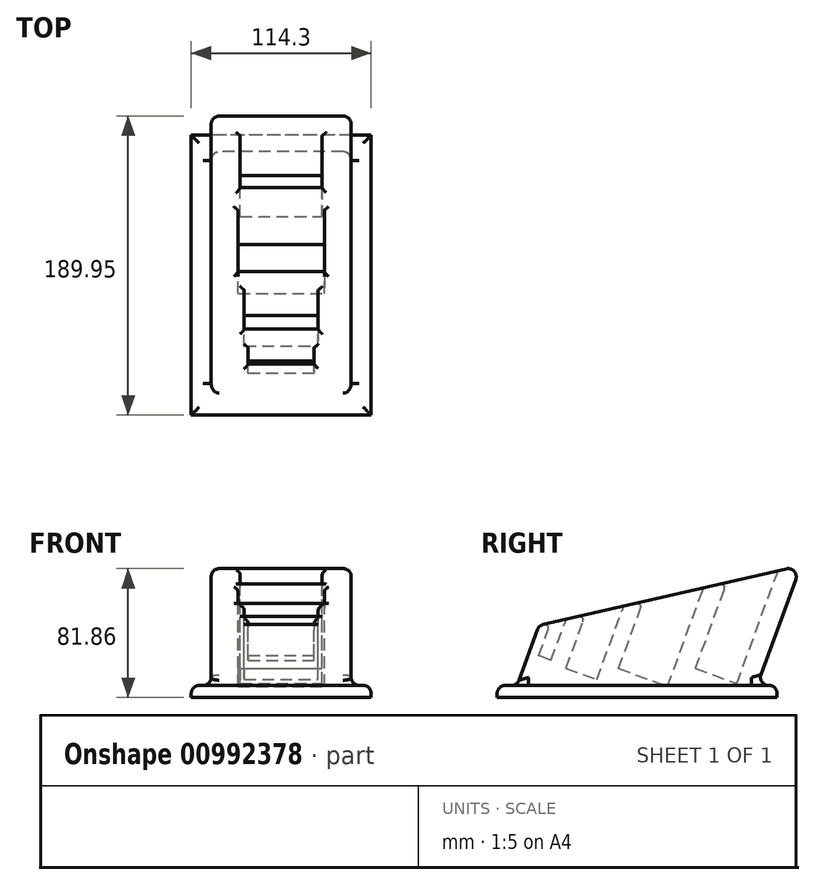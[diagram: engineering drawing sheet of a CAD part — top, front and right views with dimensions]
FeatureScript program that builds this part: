
annotation { "Feature Type Name" : "Feature", "Feature Type Description" : "" }
export const myFeature = defineFeature(function(context is Context, id is Id, definition is map)
    precondition{}
    {
        {
            var Q0;
            Q0=qCreatedBy(makeId("Right.planeOp"),FACE);
            var sketch = newSketch(context, id + "F0", { "sketchPlane" : qUnion([Q0])});
            skLineSegment(sketch, "E0.bottom", {"start": v(-88.9, 0) * mm, "end": v(88.9, 0) * mm});
            skLineSegment(sketch, "E0.left", {"start": v(-88.9, 0) * mm, "end": v(-88.9, 7.62) * mm});
            skLineSegment(sketch, "E0.right", {"start": v(88.9, 0) * mm, "end": v(88.9, 7.62) * mm});
            skLineSegment(sketch, "E1", {"start": v(-88.9, 7.62) * mm, "end": v(88.9, 7.62) * mm});
            skLineSegment(sketch, "E2", {"start": v(76.2, 7.62) * mm, "end": v(103.93, 83.82) * mm});
            skLineSegment(sketch, "E3", {"start": v(-76.2, 7.62) * mm, "end": v(-62.33, 45.72) * mm});
            skLineSegment(sketch, "E4", {"start": v(-62.33, 45.72) * mm, "end": v(103.93, 83.82) * mm});
            skSolve(sketch);
        }
        {
            var Q0;
            Q0=makeQuery(id+"F0.imprint","IMPRINT",FACE,{"disambiguationData":[TD([[makeQuery(id+"F0.imprint","IMPRINT",EDGE,{"derivedFrom":sQuery(id+"F0.wireOp",EDGE,"E0.bottom")}),1.0]])]});
            extrude(context, id + "F1", {"entities" : qUnion([Q0]), "depth" : 114.3 * mm, "offsetDistance" : 25.4 * mm, "symmetric" : true});
        }
        {
            var Q0;
            {var subQ0=sQuery(id+"F0.wireOp",EDGE,"E2");Q0=makeQuery(id+"F0.imprint","IMPRINT",FACE,{"disambiguationData":[TD([[makeQuery(id+"F0.imprint","IMPRINT",EDGE,{"derivedFrom":subQ0}),1.0]])]});}
            extrude(context, id + "F2", {"entities" : qUnion([Q0]), "operationType" : NewBodyOperationType.ADD, "depth" : 88.9 * mm, "offsetDistance" : 25.4 * mm, "symmetric" : true});
        }
        {
            var Q0;
            Q0=makeQuery(id+"F2.opExtrude","SWEPT_EDGE",EDGE,{"disambiguationData":[OSD([sQuery(id+"F0.wireOp",EDGE,"E2"),sQuery(id+"F0.wireOp",EDGE,"E4")])]});
            var Q1;
            Q1=sQuery(id+"F0.wireOp",EDGE,"E2");
            cPlane(context, id + "F3", {"entities" : qUnion([Q0, Q1]), "cplaneType" : CPlaneType.LINE_ANGLE, "offset" : 25.4 * mm, "angle" : 90 * degree, "width" : 152.4 * mm, "height" : 152.4 * mm});
        }
        {
            var Q0;
            Q0=makeQuery(id+"F2.opExtrude","SWEPT_FACE",FACE,{"disambiguationData":[OSD([sQuery(id+"F0.wireOp",EDGE,"E4")])]});
            var sketch = newSketch(context, id + "F4", { "sketchPlane" : qUnion([Q0])});
            skLineSegment(sketch, "E5.bottom", {"start": v(20.96, -42.93) * mm, "end": v(-20.96, -42.93) * mm});
            skSolve(sketch);
        }
        {
            var Q0;
            Q0=qCreatedBy(id+"F3.planeOp",FACE);
            var sketch = newSketch(context, id + "F5", { "sketchPlane" : qUnion([Q0])});
            skLineSegment(sketch, "E6.0", {"start": v(20.96, 67.81) * mm, "end": v(-20.96, 67.81) * mm});
            skLineSegment(sketch, "E7", {"start": v(-20.96, 67.81) * mm, "end": v(-20.96, 59.43) * mm});
            skLineSegment(sketch, "E8", {"start": v(-20.96, 59.43) * mm, "end": v(20.96, 59.43) * mm});
            skLineSegment(sketch, "E9", {"start": v(20.95, 59.43) * mm, "end": v(20.95, 67.81) * mm});
            skSolve(sketch);
        }
        {
            var Q0;
            Q0 = qSketchRegion(id + "F5", true);
            extrude(context, id + "F6", {"entities" : qUnion([Q0]), "operationType" : NewBodyOperationType.REMOVE, "depth" : 110.74 * mm, "offsetDistance" : 25.4 * mm});
        }
        {
            var Q0;
            {var subQ0=sQuery(id+"F0.wireOp",EDGE,"E4");Q0=makeQuery(id+"F4.imprint","IMPRINT",FACE,{"disambiguationData":[TD([[makeQuery(id+"F4.imprint","IMPRINT",EDGE,{"derivedFrom":makeQuery(id+"F2.opExtrude","CAP_EDGE",EDGE,{"disambiguationData":[OSD([subQ0])],"isStart":true})}),-1.0]])]});}
            var sketch = newSketch(context, id + "F7", { "sketchPlane" : qUnion([Q0])});
            skLineSegment(sketch, "E10", {"start": v(-23.5, -20.24) * mm, "end": v(23.5, -20.24) * mm});
            skSolve(sketch);
        }
        {
            var Q0;
            Q0=qCreatedBy(id+"F3.planeOp",FACE);
            var sketch = newSketch(context, id + "F8", { "sketchPlane" : qUnion([Q0])});
            skLineSegment(sketch, "E11.0", {"start": v(-23.5, 48.77) * mm, "end": v(23.5, 48.77) * mm});
            skLineSegment(sketch, "E12", {"start": v(-23.5, 48.77) * mm, "end": v(-23.5, 27.94) * mm});
            skLineSegment(sketch, "E13", {"start": v(-23.5, 27.94) * mm, "end": v(23.5, 27.94) * mm});
            skLineSegment(sketch, "E14", {"start": v(23.5, 27.94) * mm, "end": v(23.5, 48.77) * mm});
            skSolve(sketch);
        }
        {
            var Q0;
            Q0 = qSketchRegion(id + "F8", true);
            extrude(context, id + "F9", {"entities" : qUnion([Q0]), "operationType" : NewBodyOperationType.REMOVE, "depth" : 112.27 * mm, "offsetDistance" : 25.4 * mm});
        }
        {
            var Q0;
            {var subQ0=sQuery(id+"F0.wireOp",EDGE,"E4");Q0=makeQuery(id+"F4.imprint","IMPRINT",FACE,{"disambiguationData":[TD([[makeQuery(id+"F4.imprint","IMPRINT",EDGE,{"derivedFrom":makeQuery(id+"F2.opExtrude","CAP_EDGE",EDGE,{"disambiguationData":[OSD([subQ0])],"isStart":true})}),-1.0]])]});}
            var sketch = newSketch(context, id + "F10", { "sketchPlane" : qUnion([Q0])});
            skLineSegment(sketch, "E15", {"start": v(-27.43, 17.27) * mm, "end": v(27.43, 17.27) * mm});
            skLineSegment(sketch, "E16", {"start": v(0, 85.1) * mm, "end": v(0, -16.61) * mm, "construction": true});
            skSolve(sketch);
        }
        {
            var Q0;
            Q0=qCreatedBy(id+"F3.planeOp",FACE);
            var sketch = newSketch(context, id + "F11", { "sketchPlane" : qUnion([Q0])});
            skLineSegment(sketch, "E17.0", {"start": v(-27.43, 17.28) * mm, "end": v(27.43, 17.28) * mm});
            skLineSegment(sketch, "E18", {"start": v(-27.43, 17.28) * mm, "end": v(-27.43, -15.74) * mm});
            skLineSegment(sketch, "E19", {"start": v(-27.43, -15.74) * mm, "end": v(27.43, -15.74) * mm});
            skLineSegment(sketch, "E20", {"start": v(27.43, -15.74) * mm, "end": v(27.43, 17.28) * mm});
            skSolve(sketch);
        }
        {
            var Q0;
            Q0 = qSketchRegion(id + "F11", true);
            extrude(context, id + "F12", {"entities" : qUnion([Q0]), "operationType" : NewBodyOperationType.REMOVE, "depth" : 101.1 * mm, "offsetDistance" : 25.4 * mm});
        }
        {
            var Q0;
            {var subQ0=sQuery(id+"F0.wireOp",EDGE,"E4");Q0=makeQuery(id+"F4.imprint","IMPRINT",FACE,{"disambiguationData":[TD([[makeQuery(id+"F4.imprint","IMPRINT",EDGE,{"derivedFrom":makeQuery(id+"F2.opExtrude","CAP_EDGE",EDGE,{"disambiguationData":[OSD([subQ0])],"isStart":true})}),-1.0]])]});}
            var sketch = newSketch(context, id + "F13", { "sketchPlane" : qUnion([Q0])});
            skLineSegment(sketch, "E21", {"start": v(-26.04, 71.84) * mm, "end": v(26.04, 71.84) * mm});
            skSolve(sketch);
        }
        {
            var Q0;
            Q0=qCreatedBy(id+"F3.planeOp",FACE);
            var sketch = newSketch(context, id + "F14", { "sketchPlane" : qUnion([Q0])});
            skLineSegment(sketch, "E22.0", {"start": v(-26.04, -28.54) * mm, "end": v(26.04, -28.54) * mm});
            skLineSegment(sketch, "E23", {"start": v(-26.03, -28.54) * mm, "end": v(-26.03, -56.48) * mm});
            skLineSegment(sketch, "E24", {"start": v(-26.03, -56.48) * mm, "end": v(26.04, -56.48) * mm});
            skLineSegment(sketch, "E25", {"start": v(26.04, -56.48) * mm, "end": v(26.04, -28.54) * mm});
            skSolve(sketch);
        }
        {
            var Q0;
            Q0 = qSketchRegion(id + "F14", true);
            extrude(context, id + "F15", {"entities" : qUnion([Q0]), "operationType" : NewBodyOperationType.REMOVE, "depth" : 84.33 * mm, "offsetDistance" : 25.4 * mm});
        }
        {
            var Q0;
            Q0=makeQuery(id+"F2.opExtrude","CAP_EDGE",EDGE,{"disambiguationData":[OSD([sQuery(id+"F0.wireOp",EDGE,"E4")])],"isStart":false});
            var Q1;
            Q1=makeQuery(id+"F2.opExtrude","SWEPT_EDGE",EDGE,{"disambiguationData":[OSD([sQuery(id+"F0.wireOp",EDGE,"E3"),sQuery(id+"F0.wireOp",EDGE,"E4")])]});
            var Q2;
            Q2=makeQuery(id+"F2.opExtrude","CAP_FACE",FACE,{"disambiguationData":[OSD([sQuery(id+"F0.wireOp",EDGE,"E1"),sQuery(id+"F0.wireOp",EDGE,"E2"),sQuery(id+"F0.wireOp",EDGE,"E3"),sQuery(id+"F0.wireOp",EDGE,"E4")])],"isStart":false});
            var Q3;
            Q3=makeQuery(id+"F2.opExtrude","SWEPT_EDGE",EDGE,{"disambiguationData":[OSD([sQuery(id+"F0.wireOp",EDGE,"E2"),sQuery(id+"F0.wireOp",EDGE,"E4")])]});
            var Q4;
            Q4=makeQuery(id+"F2.opExtrude","CAP_FACE",FACE,{"disambiguationData":[OSD([sQuery(id+"F0.wireOp",EDGE,"E1"),sQuery(id+"F0.wireOp",EDGE,"E2"),sQuery(id+"F0.wireOp",EDGE,"E3"),sQuery(id+"F0.wireOp",EDGE,"E4")])],"isStart":true});
            var Q5;
            Q5=makeQuery(id+"F1.opExtrude","SWEPT_FACE",FACE,{"disambiguationData":[OSD([sQuery(id+"F0.wireOp",EDGE,"E1")])]});
            fillet(context, id + "F16", {"entities" : qUnion([Q0, Q1, Q2, Q3, Q4, Q5]), "tangentPropagation" : true, "radius" : 5.08 * mm, "defaultsChanged" : false, "vertexSettings" : [], "allowEdgeOverflow" : false});
        }
        {
            var Q0;
            Q0=makeQuery(id+"F15.boolean.opBoolean","INTERSECT",EDGE,{"derivedFrom":[makeQuery(id+"F2.opExtrude","SWEPT_FACE",FACE,{"disambiguationData":[OSD([sQuery(id+"F0.wireOp",EDGE,"E4")])]}),makeQuery(id+"F15.opExtrude","SWEPT_FACE",FACE,{"disambiguationData":[OSD([sQuery(id+"F14.wireOp",EDGE,"E22.0")])]})]});
            var Q1;
            Q1=makeQuery(id+"F15.boolean.opBoolean","INTERSECT",EDGE,{"derivedFrom":[makeQuery(id+"F2.opExtrude","SWEPT_FACE",FACE,{"disambiguationData":[OSD([sQuery(id+"F0.wireOp",EDGE,"E4")])]}),makeQuery(id+"F15.opExtrude","SWEPT_FACE",FACE,{"disambiguationData":[OSD([sQuery(id+"F14.wireOp",EDGE,"E24")])]})]});
            var Q2;
            Q2=makeQuery(id+"F15.boolean.opBoolean","INTERSECT",EDGE,{"derivedFrom":[makeQuery(id+"F2.opExtrude","SWEPT_FACE",FACE,{"disambiguationData":[OSD([sQuery(id+"F0.wireOp",EDGE,"E4")])]}),makeQuery(id+"F15.opExtrude","SWEPT_FACE",FACE,{"disambiguationData":[OSD([sQuery(id+"F14.wireOp",EDGE,"E25")])]})]});
            var Q3;
            Q3=makeQuery(id+"F15.boolean.opBoolean","INTERSECT",EDGE,{"derivedFrom":[makeQuery(id+"F2.opExtrude","SWEPT_FACE",FACE,{"disambiguationData":[OSD([sQuery(id+"F0.wireOp",EDGE,"E4")])]}),makeQuery(id+"F15.opExtrude","SWEPT_FACE",FACE,{"disambiguationData":[OSD([sQuery(id+"F14.wireOp",EDGE,"E23")])]})]});
            var Q4;
            Q4=makeQuery(id+"F12.boolean.opBoolean","INTERSECT",EDGE,{"derivedFrom":[makeQuery(id+"F2.opExtrude","SWEPT_FACE",FACE,{"disambiguationData":[OSD([sQuery(id+"F0.wireOp",EDGE,"E4")])]}),makeQuery(id+"F12.opExtrude","SWEPT_FACE",FACE,{"disambiguationData":[OSD([sQuery(id+"F11.wireOp",EDGE,"E18")])]})]});
            var Q5;
            Q5=makeQuery(id+"F12.boolean.opBoolean","INTERSECT",EDGE,{"derivedFrom":[makeQuery(id+"F2.opExtrude","SWEPT_FACE",FACE,{"disambiguationData":[OSD([sQuery(id+"F0.wireOp",EDGE,"E4")])]}),makeQuery(id+"F12.opExtrude","SWEPT_FACE",FACE,{"disambiguationData":[OSD([sQuery(id+"F11.wireOp",EDGE,"E19")])]})]});
            var Q6;
            Q6=makeQuery(id+"F12.boolean.opBoolean","INTERSECT",EDGE,{"derivedFrom":[makeQuery(id+"F2.opExtrude","SWEPT_FACE",FACE,{"disambiguationData":[OSD([sQuery(id+"F0.wireOp",EDGE,"E4")])]}),makeQuery(id+"F12.opExtrude","SWEPT_FACE",FACE,{"disambiguationData":[OSD([sQuery(id+"F11.wireOp",EDGE,"E20")])]})]});
            var Q7;
            Q7=makeQuery(id+"F12.boolean.opBoolean","INTERSECT",EDGE,{"derivedFrom":[makeQuery(id+"F2.opExtrude","SWEPT_FACE",FACE,{"disambiguationData":[OSD([sQuery(id+"F0.wireOp",EDGE,"E4")])]}),makeQuery(id+"F12.opExtrude","SWEPT_FACE",FACE,{"disambiguationData":[OSD([sQuery(id+"F11.wireOp",EDGE,"E17.0")])]})]});
            var Q8;
            Q8=makeQuery(id+"F9.boolean.opBoolean","INTERSECT",EDGE,{"derivedFrom":[makeQuery(id+"F2.opExtrude","SWEPT_FACE",FACE,{"disambiguationData":[OSD([sQuery(id+"F0.wireOp",EDGE,"E4")])]}),makeQuery(id+"F9.opExtrude","SWEPT_FACE",FACE,{"disambiguationData":[OSD([sQuery(id+"F8.wireOp",EDGE,"E13")])]})]});
            var Q9;
            Q9=makeQuery(id+"F9.boolean.opBoolean","INTERSECT",EDGE,{"derivedFrom":[makeQuery(id+"F2.opExtrude","SWEPT_FACE",FACE,{"disambiguationData":[OSD([sQuery(id+"F0.wireOp",EDGE,"E4")])]}),makeQuery(id+"F9.opExtrude","SWEPT_FACE",FACE,{"disambiguationData":[OSD([sQuery(id+"F8.wireOp",EDGE,"E14")])]})]});
            var Q10;
            Q10=makeQuery(id+"F9.boolean.opBoolean","INTERSECT",EDGE,{"derivedFrom":[makeQuery(id+"F2.opExtrude","SWEPT_FACE",FACE,{"disambiguationData":[OSD([sQuery(id+"F0.wireOp",EDGE,"E4")])]}),makeQuery(id+"F9.opExtrude","SWEPT_FACE",FACE,{"disambiguationData":[OSD([sQuery(id+"F8.wireOp",EDGE,"E11.0")])]})]});
            var Q11;
            Q11=makeQuery(id+"F9.boolean.opBoolean","INTERSECT",EDGE,{"derivedFrom":[makeQuery(id+"F2.opExtrude","SWEPT_FACE",FACE,{"disambiguationData":[OSD([sQuery(id+"F0.wireOp",EDGE,"E4")])]}),makeQuery(id+"F9.opExtrude","SWEPT_FACE",FACE,{"disambiguationData":[OSD([sQuery(id+"F8.wireOp",EDGE,"E12")])]})]});
            var Q12;
            Q12=makeQuery(id+"F6.boolean.opBoolean","INTERSECT",EDGE,{"derivedFrom":[makeQuery(id+"F2.opExtrude","SWEPT_FACE",FACE,{"disambiguationData":[OSD([sQuery(id+"F0.wireOp",EDGE,"E4")])]}),makeQuery(id+"F6.opExtrude","SWEPT_FACE",FACE,{"disambiguationData":[OSD([sQuery(id+"F5.wireOp",EDGE,"E8")])]})]});
            var Q13;
            Q13=makeQuery(id+"F6.boolean.opBoolean","INTERSECT",EDGE,{"derivedFrom":[makeQuery(id+"F2.opExtrude","SWEPT_FACE",FACE,{"disambiguationData":[OSD([sQuery(id+"F0.wireOp",EDGE,"E4")])]}),makeQuery(id+"F6.opExtrude","SWEPT_FACE",FACE,{"disambiguationData":[OSD([sQuery(id+"F5.wireOp",EDGE,"E7")])]})]});
            var Q14;
            Q14=makeQuery(id+"F6.boolean.opBoolean","INTERSECT",EDGE,{"derivedFrom":[makeQuery(id+"F2.opExtrude","SWEPT_FACE",FACE,{"disambiguationData":[OSD([sQuery(id+"F0.wireOp",EDGE,"E4")])]}),makeQuery(id+"F6.opExtrude","SWEPT_FACE",FACE,{"disambiguationData":[OSD([sQuery(id+"F5.wireOp",EDGE,"E9")])]})]});
            var Q15;
            Q15=makeQuery(id+"F6.boolean.opBoolean","INTERSECT",EDGE,{"derivedFrom":[makeQuery(id+"F2.opExtrude","SWEPT_FACE",FACE,{"disambiguationData":[OSD([sQuery(id+"F0.wireOp",EDGE,"E4")])]}),makeQuery(id+"F6.opExtrude","SWEPT_FACE",FACE,{"disambiguationData":[OSD([sQuery(id+"F5.wireOp",EDGE,"E6.0")])]})]});
            fillet(context, id + "F17", {"entities" : qUnion([Q0, Q1, Q2, Q3, Q4, Q5, Q6, Q7, Q8, Q9, Q10, Q11, Q12, Q13, Q14, Q15]), "tangentPropagation" : true, "radius" : 2.54 * mm, "defaultsChanged" : false, "vertexSettings" : [], "allowEdgeOverflow" : false});
        }
    });
